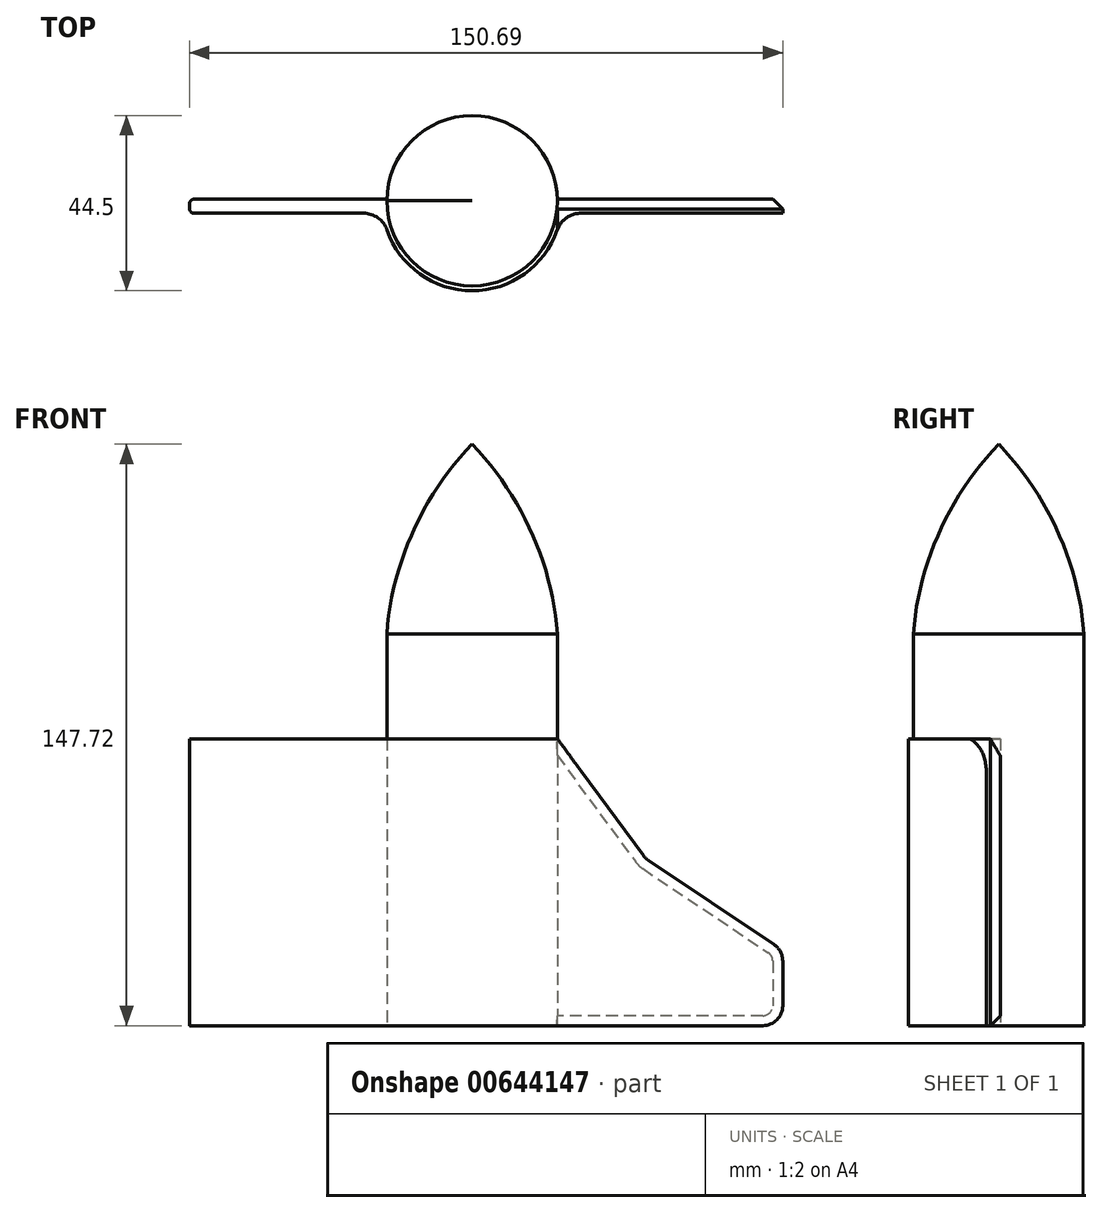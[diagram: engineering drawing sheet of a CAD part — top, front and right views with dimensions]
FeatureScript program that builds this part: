
annotation { "Feature Type Name" : "Feature", "Feature Type Description" : "" }
export const myFeature = defineFeature(function(context is Context, id is Id, definition is map)
    precondition{}
    {
        {
            var Q0;
            Q0=qCreatedBy(makeId("Front.planeOp"),FACE);
            var sketch = newSketch(context, id + "F0", { "sketchPlane" : qUnion([Q0])});
            skLineSegment(sketch, "E0", {"start": v(0, 0) * mm, "end": v(-15.73, 0) * mm});
            skLineSegment(sketch, "E1", {"start": v(-15.73, 0) * mm, "end": v(0, 77.1) * mm});
            skLineSegment(sketch, "E2", {"start": v(0, 77.1) * mm, "end": v(0, 0) * mm});
            skFitSpline(sketch, "E3", {"points": [v(0, 77.1) * mm, v(-15.73, 0) * mm, v(33.71, -30) * mm, v(29.99, 0) * mm, v(6.52, 33.7) * mm, v(29.61, 90.7) * mm, v(0, 77.1) * mm]});
            skSolve(sketch);
        }
        {
            var Q0;
            Q0=makeQuery(id+"F0.imprint","IMPRINT",FACE,{"disambiguationData":[TD([[makeQuery(id+"F0.imprint","IMPRINT",EDGE,{"derivedFrom":sQuery(id+"F0.wireOp",EDGE,"E1")}),1.0]])]});
            var Q1;
            Q1=makeQuery(id+"F0.imprint","IMPRINT",FACE,{"disambiguationData":[TD([[makeQuery(id+"F0.imprint","IMPRINT",EDGE,{"derivedFrom":sQuery(id+"F0.wireOp",EDGE,"E0")}),-1.0]])]});
            var Q2;
            Q2=sQuery(id+"F0.wireOp",EDGE,"E2");
            revolve(context, id + "F1", {"entities" : qUnion([Q0, Q1]), "axis" : qUnion([Q2]), "revolveType" : RevolveType.FULL});
        }
        {
            var Q0;
            Q0=makeQuery(id+"F1.opRevolve","SWEPT_FACE",FACE,{"disambiguationData":[OSD([sQuery(id+"F0.wireOp",EDGE,"E0")])]});
            var sketch = newSketch(context, id + "F2", { "sketchPlane" : qUnion([Q0])});
            skCircle(sketch, "E4", {"center": v(0, 0) * mm, "radius": 43.99 * mm});
            skSolve(sketch);
        }
        {
            var Q0;
            Q0=makeQuery(id+"F2.imprint","IMPRINT",FACE,{"disambiguationData":[TD([[makeQuery(id+"F2.imprint","IMPRINT",EDGE,{"derivedFrom":sQuery(id+"F2.wireOp",EDGE,"E4")}),1.0]])]});
            var Q1;
            Q1=makeQuery(id+"F2.imprint","IMPRINT",FACE,{"disambiguationData":[TD([[makeQuery(id+"F2.imprint","IMPRINT",EDGE,{"derivedFrom":makeQuery(id+"F1.opRevolve","SWEPT_EDGE",EDGE,{"disambiguationData":[OSD([sQuery(id+"F0.wireOp",EDGE,"E0"),sQuery(id+"F0.wireOp",EDGE,"E1"),sQuery(id+"F0.wireOp",EDGE,"E3")])]})}),-1.0]])]});
            extrude(context, id + "F3", {"entities" : qUnion([Q0, Q1]), "operationType" : NewBodyOperationType.REMOVE, "oppositeDirection" : true, "depth" : 28.96 * mm, "offsetDistance" : 25.4 * mm});
        }
        {
            var Q0;
            Q0=makeQuery(id+"F3.boolean.opBoolean","COPY",FACE,{"derivedFrom":makeQuery(id+"F3.opExtrude","CAP_FACE",FACE,{"disambiguationData":[OSD([sQuery(id+"F2.wireOp",EDGE,"E4")])],"isStart":false})});
            extrude(context, id + "F4", {"entities" : qUnion([Q0]), "depth" : 99.57 * mm, "offsetDistance" : 25.4 * mm});
        }
        {
            var Q0;
            Q0=makeQuery(id+"F4.opExtrude","CAP_FACE",FACE,{"disambiguationData":[OSD([sQuery(id+"F2.wireOp",EDGE,"E4")])],"isStart":false});
            var sketch = newSketch(context, id + "F5", { "sketchPlane" : qUnion([Q0])});
            skArc(sketch, "E5", {"start": v(21.61, 7.44) * mm, "mid": v(0, 22.86) * mm, "end": v(-21.61, 7.44) * mm});
            skLineSegment(sketch, "E6", {"start": v(-26.75, 0) * mm, "end": v(26.75, 0) * mm});
            skLineSegment(sketch, "E7", {"start": v(-70.65, -0.4) * mm, "end": v(78.92, -0.4) * mm});
            skLineSegment(sketch, "E8", {"start": v(80.05, 0.73) * mm, "end": v(80.05, 2.03) * mm});
            skLineSegment(sketch, "E9", {"start": v(-27.62, 3.16) * mm, "end": v(-70.65, 3.16) * mm});
            skLineSegment(sketch, "E10", {"start": v(-71.77, 2.03) * mm, "end": v(-71.77, 0.73) * mm});
            skPoint(sketch, "E11.newPointA", {"position": v(-22.86, -0.4) * mm});
            skArc(sketch, "E11.filletArc", {"start": v(-27.62, 3.16) * mm, "mid": v(-23.93, 4.34) * mm, "end": v(-21.61, 7.44) * mm});
            skLineSegment(sketch, "E12", {"start": v(78.92, 3.16) * mm, "end": v(27.62, 3.16) * mm});
            skArc(sketch, "E13.filletArc", {"start": v(21.61, 7.44) * mm, "mid": v(23.93, 4.34) * mm, "end": v(27.62, 3.16) * mm});
            skPoint(sketch, "E14.visualSharp", {"position": v(-71.77, 3.16) * mm});
            skArc(sketch, "E14.filletArc", {"start": v(-70.65, 3.16) * mm, "mid": v(-71.44, 2.83) * mm, "end": v(-71.77, 2.03) * mm});
            skPoint(sketch, "E15.visualSharp", {"position": v(-71.77, -0.4) * mm});
            skArc(sketch, "E15.filletArc", {"start": v(-71.77, 0.73) * mm, "mid": v(-71.44, -0.07) * mm, "end": v(-70.65, -0.4) * mm});
            skPoint(sketch, "E16.visualSharp", {"position": v(80.05, -0.4) * mm});
            skArc(sketch, "E16.filletArc", {"start": v(78.92, -0.4) * mm, "mid": v(79.72, -0.07) * mm, "end": v(80.05, 0.73) * mm});
            skPoint(sketch, "E17.visualSharp", {"position": v(80.05, 3.16) * mm});
            skArc(sketch, "E17.filletArc", {"start": v(80.05, 2.03) * mm, "mid": v(79.72, 2.83) * mm, "end": v(78.92, 3.16) * mm});
            skSolve(sketch);
        }
        {
            var Q0;
            Q0=makeQuery(id+"F5.imprint","IMPRINT",FACE,{"disambiguationData":[TD([[makeQuery(id+"F5.imprint","IMPRINT",EDGE,{"derivedFrom":sQuery(id+"F5.wireOp",EDGE,"E5")}),1.0]])]});
            extrude(context, id + "F6", {"entities" : qUnion([Q0]), "operationType" : NewBodyOperationType.ADD, "oppositeDirection" : true, "depth" : 72.9 * mm, "offsetDistance" : 25.4 * mm});
        }
        {
            var Q0;
            {var subQ0=sQuery(id+"F5.wireOp",EDGE,"E7");Q0=makeQuery(id+"F6.opExtrude","SWEPT_FACE",FACE,{"disambiguationData":[OSD([subQ0]),TDD([makeQuery(id+"F5.imprint","IMPRINT",EDGE,{"disambiguationData":[TD([[makeQuery(id+"F5.imprint","INTERSECT",VERTEX,{"derivedFrom":[subQ0,sQuery(id+"F5.wireOp",EDGE,"E16.filletArc")]}),1.0]])],"derivedFrom":subQ0})])]});}
            var sketch = newSketch(context, id + "F7", { "sketchPlane" : qUnion([Q0])});
            skPoint(sketch, "E18", {"position": v(-21.64, 2.29) * mm});
            skLineSegment(sketch, "E19", {"start": v(-21.64, 2.29) * mm, "end": v(-43.51, -27.4) * mm});
            skLineSegment(sketch, "E20", {"start": v(-44.78, -28.6) * mm, "end": v(-76.67, -49.97) * mm});
            skLineSegment(sketch, "E21", {"start": v(-78.92, -54.19) * mm, "end": v(-78.92, -65.53) * mm});
            skLineSegment(sketch, "E22", {"start": v(-73.84, -70.61) * mm, "end": v(-21.64, -70.61) * mm});
            skLineSegment(sketch, "E23", {"start": v(-21.64, -70.61) * mm, "end": v(-21.64, 2.29) * mm});
            skPoint(sketch, "E24.visualSharp", {"position": v(-78.92, -70.61) * mm});
            skArc(sketch, "E24.filletArc", {"start": v(-78.92, -65.53) * mm, "mid": v(-77.43, -69.12) * mm, "end": v(-73.84, -70.61) * mm});
            skPoint(sketch, "E25.visualSharp", {"position": v(-78.92, -51.48) * mm});
            skArc(sketch, "E25.filletArc", {"start": v(-76.67, -49.97) * mm, "mid": v(-78.32, -51.8) * mm, "end": v(-78.92, -54.19) * mm});
            skPoint(sketch, "E26.visualSharp", {"position": v(-44.04, -28.11) * mm});
            skArc(sketch, "E26.filletArc", {"start": v(-44.78, -28.6) * mm, "mid": v(-44.1, -28.06) * mm, "end": v(-43.51, -27.4) * mm});
            skSolve(sketch);
        }
        {
            var Q0;
            Q0=makeQuery(id+"F7.imprint","IMPRINT",FACE,{"disambiguationData":[TD([[makeQuery(id+"F7.imprint","IMPRINT",EDGE,{"derivedFrom":sQuery(id+"F7.wireOp",EDGE,"E19")}),-1.0]])]});
            var Q1;
            {var subQ0=sQuery(id+"F7.wireOp",EDGE,"E24.filletArc");Q1=makeQuery(id+"F7.imprint","IMPRINT",FACE,{"disambiguationData":[TD([[makeQuery(id+"F7.imprint","IMPRINT",EDGE,{"derivedFrom":subQ0}),-1.0]])]});}
            extrude(context, id + "F8", {"entities" : qUnion([Q0, Q1]), "operationType" : NewBodyOperationType.REMOVE, "endBound" : BoundingType.THROUGH_ALL, "oppositeDirection" : true, "depth" : 25.4 * mm, "offsetDistance" : 25.4 * mm});
        }
        {
            var Q0;
            {var subQ0=sQuery(id+"F5.wireOp",EDGE,"E8");var subQ1=sQuery(id+"F5.wireOp",EDGE,"E16.filletArc");var subQ2=sQuery(id+"F5.wireOp",EDGE,"E17.filletArc");var subQ3=sQuery(id+"F5.wireOp",EDGE,"E7");var subQ4=sQuery(id+"F2.wireOp",EDGE,"E4");var subQ5=sQuery(id+"F0.wireOp",EDGE,"E3");Q0=makeQuery(id+"F8.boolean.opBoolean","SPLIT",FACE,{"disambiguationData":[TD([makeQuery(id+"F6.opExtrude","SWEPT_FACE",FACE,{"disambiguationData":[OSD([subQ0])]})])],"derivedFrom":makeQuery(id+"F6.opExtrude","CAP_FACE",FACE,{"disambiguationData":[OSD([subQ5,subQ4,sQuery(id+"F5.wireOp",EDGE,"E5"),subQ3,subQ0,sQuery(id+"F5.wireOp",EDGE,"E9"),sQuery(id+"F5.wireOp",EDGE,"E10"),sQuery(id+"F5.wireOp",EDGE,"E11.filletArc"),sQuery(id+"F5.wireOp",EDGE,"E12"),sQuery(id+"F5.wireOp",EDGE,"E13.filletArc"),sQuery(id+"F5.wireOp",EDGE,"E14.filletArc"),sQuery(id+"F5.wireOp",EDGE,"E15.filletArc"),subQ1,subQ2])],"isStart":false})});}
            extrude(context, id + "F9", {"entities" : qUnion([Q0]), "operationType" : NewBodyOperationType.REMOVE, "endBound" : BoundingType.THROUGH_ALL, "oppositeDirection" : true, "depth" : 25.4 * mm, "offsetDistance" : 25.4 * mm});
        }
        {
            var Q0;
            {var subQ0=sQuery(id+"F5.wireOp",EDGE,"E16.filletArc");var subQ1=sQuery(id+"F5.wireOp",EDGE,"E7");Q0=makeQuery(id+"F9.boolean.opBoolean","MERGE",EDGE,{"derivedFrom":[makeQuery(id+"F8.boolean.opBoolean","SPLIT",EDGE,{"derivedFrom":makeQuery(id+"F6.opExtrude","SWEPT_EDGE",EDGE,{"disambiguationData":[OSD([subQ1,subQ0])]})}),makeQuery(id+"F9.opExtrude","SWEPT_EDGE",EDGE,{"disambiguationData":[OSD([subQ1,subQ0])]})]});}
            chamfer(context, id + "F10", {"entities" : qUnion([Q0]), "width" : 2.54 * mm, "tangentPropagation" : true});
        }
    });
